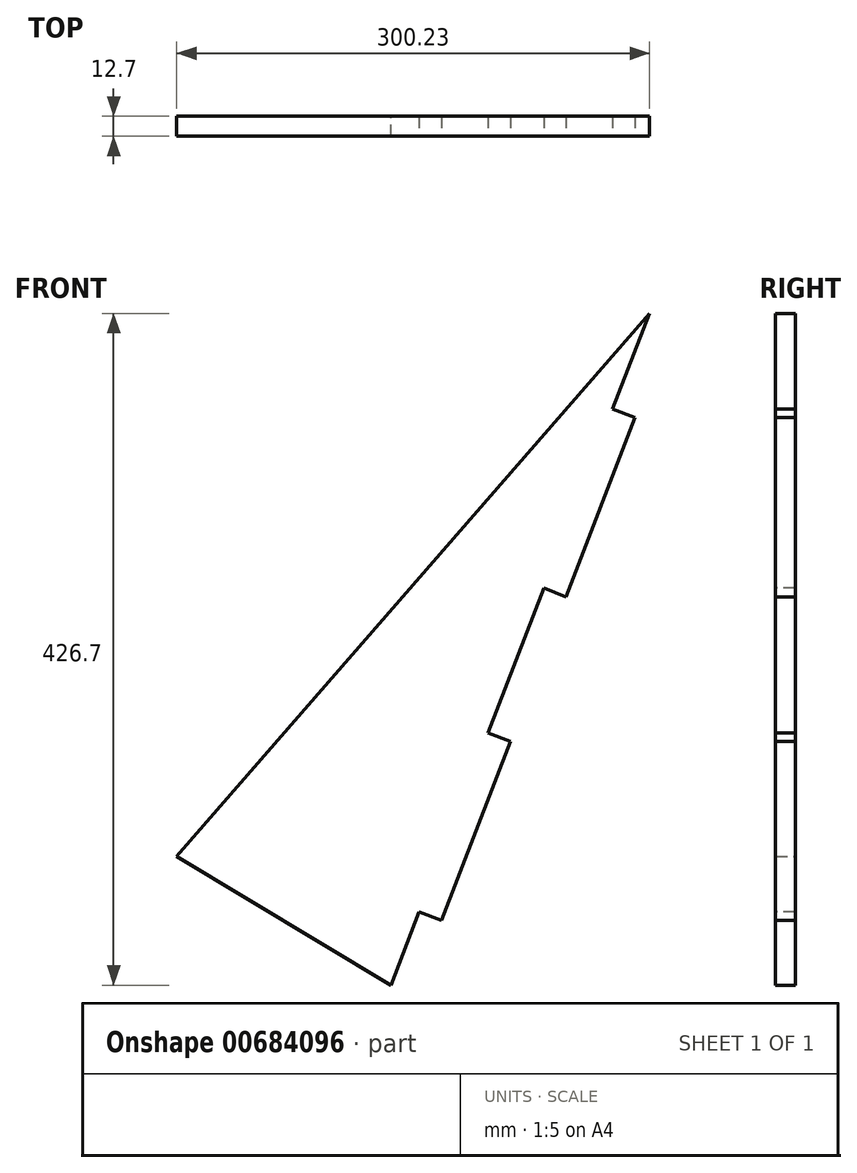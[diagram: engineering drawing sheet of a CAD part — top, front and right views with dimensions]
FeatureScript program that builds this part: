
annotation { "Feature Type Name" : "Feature", "Feature Type Description" : "" }
export const myFeature = defineFeature(function(context is Context, id is Id, definition is map)
    precondition{}
    {
        {
            var Q0;
            Q0=qCreatedBy(makeId("Front.planeOp"),FACE);
            var sketch = newSketch(context, id + "F0", { "sketchPlane" : qUnion([Q0])});
            skLineSegment(sketch, "E0", {"start": v(142.23, 210.82) * mm, "end": v(-158, -134) * mm});
            skLineSegment(sketch, "E1", {"start": v(-158, -134) * mm, "end": v(-21.96, -215.88) * mm});
            skLineSegment(sketch, "E2", {"start": v(-21.96, -215.88) * mm, "end": v(142.23, 210.82) * mm});
            skSolve(sketch);
        }
        {
            var Q0;
            Q0 = qSketchRegion(id + "F0", true);
            extrude(context, id + "F1", {"entities" : qUnion([Q0]), "depth" : 12.7 * mm, "offsetDistance" : 25.4 * mm});
        }
        {
            var Q0;
            Q0=makeQuery(id+"F1.opExtrude","SWEPT_FACE",FACE,{"disambiguationData":[OSD([sQuery(id+"F0.wireOp",EDGE,"E2")])]});
            var sketch = newSketch(context, id + "F2", { "sketchPlane" : qUnion([Q0])});
            skLineSegment(sketch, "E3.bottom", {"start": v(0, 182.74) * mm, "end": v(-12.7, 182.74) * mm});
            skLineSegment(sketch, "E3.top", {"start": v(0, 60.82) * mm, "end": v(-12.7, 60.82) * mm});
            skLineSegment(sketch, "E3.left", {"start": v(0, 182.74) * mm, "end": v(0, 60.82) * mm});
            skLineSegment(sketch, "E3.right", {"start": v(-12.7, 182.74) * mm, "end": v(-12.7, 60.82) * mm});
            skLineSegment(sketch, "E4.bottom", {"start": v(0, -37.54) * mm, "end": v(-12.7, -37.54) * mm});
            skLineSegment(sketch, "E4.top", {"start": v(0, -159.46) * mm, "end": v(-12.7, -159.46) * mm});
            skLineSegment(sketch, "E4.left", {"start": v(0, -37.54) * mm, "end": v(0, -159.46) * mm});
            skLineSegment(sketch, "E4.right", {"start": v(-12.7, -37.54) * mm, "end": v(-12.7, -159.46) * mm});
            skSolve(sketch);
        }
        {
            var Q0;
            Q0 = qSketchRegion(id + "F2", true);
            extrude(context, id + "F3", {"entities" : qUnion([Q0]), "operationType" : NewBodyOperationType.ADD, "depth" : 15.24 * mm, "offsetDistance" : 25.4 * mm});
        }
    });
